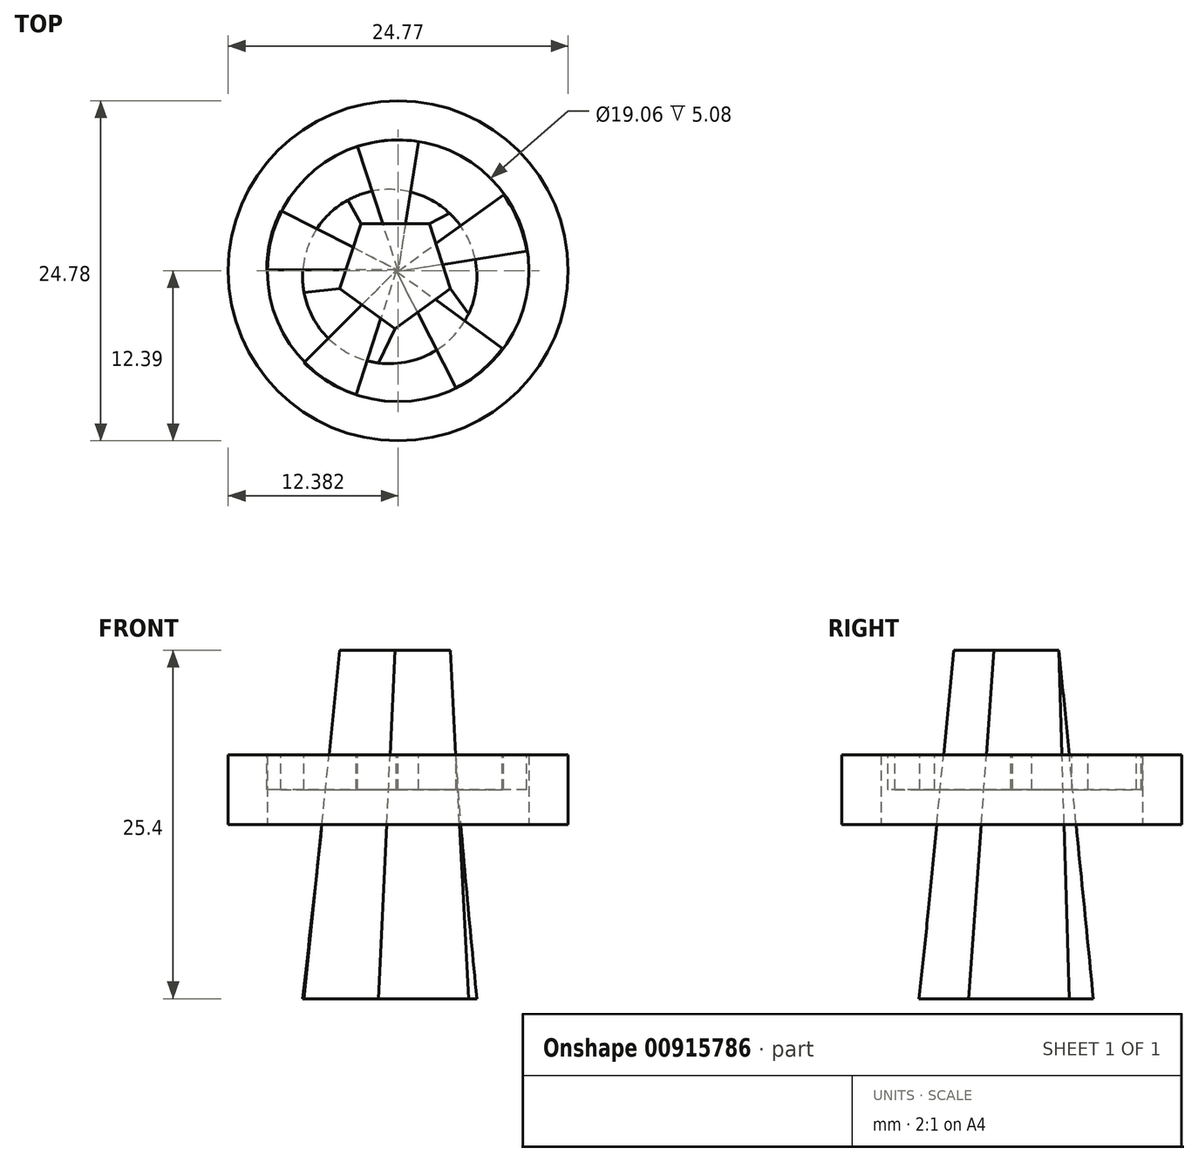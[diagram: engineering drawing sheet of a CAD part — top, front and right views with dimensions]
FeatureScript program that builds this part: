
annotation { "Feature Type Name" : "Feature", "Feature Type Description" : "" }
export const myFeature = defineFeature(function(context is Context, id is Id, definition is map)
    precondition{}
    {
        {
            var Q0;
            Q0=qCreatedBy(makeId("Top.planeOp"),FACE);
            var sketch = newSketch(context, id + "F0", { "sketchPlane" : qUnion([Q0])});
            skCircle(sketch, "E0", {"center": v(-46, -0.42) * mm, "radius": 6.35 * mm});
            skSolve(sketch);
        }
        {
            var Q0;
            Q0=qCreatedBy(makeId("Front.planeOp"),FACE);
            var sketch = newSketch(context, id + "F1", { "sketchPlane" : qUnion([Q0])});
            skLineSegment(sketch, "E1", {"start": v(-45.45, 0) * mm, "end": v(-45.45, 25.4) * mm});
            skLineSegment(sketch, "E2", {"start": v(-45.45, 12.7) * mm, "end": v(-32.74, 12.7) * mm});
            skSolve(sketch);
        }
        {
            var Q0;
            Q0=sQuery(id+"F1.wireOp",EDGE,"E1");
            var Q1;
            Q1=sQuery(id+"F1.wireOp",VERTEX,"E1.end");
            cPlane(context, id + "F2", {"entities" : qUnion([Q0, Q1]), "cplaneType" : CPlaneType.CURVE_POINT, "offset" : 25.4 * mm, "width" : 152.4 * mm, "height" : 152.4 * mm});
        }
        {
            var Q0;
            Q0=qCreatedBy(id+"F2.planeOp",FACE);
            var sketch = newSketch(context, id + "F3", { "sketchPlane" : qUnion([Q0])});
            skCircle(sketch, "E3.cCircle", {"center": v(-45.6, 0) * mm, "radius": 3.43 * mm, "construction": true});
            skLineSegment(sketch, "E3.0", {"start": v(-48.1, 3.43) * mm, "end": v(-43.11, 3.43) * mm});
            skLineSegment(sketch, "E3.1", {"start": v(-43.11, 3.43) * mm, "end": v(-41.58, -1.3) * mm});
            skLineSegment(sketch, "E3.2", {"start": v(-41.58, -1.3) * mm, "end": v(-45.6, -4.23) * mm});
            skLineSegment(sketch, "E3.3", {"start": v(-45.6, -4.23) * mm, "end": v(-49.63, -1.3) * mm});
            skLineSegment(sketch, "E3.4", {"start": v(-49.63, -1.3) * mm, "end": v(-48.1, 3.43) * mm});
            skPoint(sketch, "E3.0.midPoint", {"position": v(-45.6, 3.43) * mm});
            skSolve(sketch);
        }
        {
            var Q0;
            Q0=makeQuery(id+"F0.imprint","IMPRINT",FACE,{"disambiguationData":[TD([[makeQuery(id+"F0.imprint","IMPRINT",EDGE,{"derivedFrom":sQuery(id+"F0.wireOp",EDGE,"E0")}),1.0]])]});
            var Q1;
            Q1=makeQuery(id+"F3.imprint","IMPRINT",FACE,{"disambiguationData":[TD([[makeQuery(id+"F3.imprint","IMPRINT",EDGE,{"derivedFrom":sQuery(id+"F3.wireOp",EDGE,"E3.0")}),-1.0]])]});
            loft(context, id + "F4", {"sheetProfilesArray" : [{ "sheetProfileEntities" : qUnion([Q0]) }, { "sheetProfileEntities" : qUnion([Q1]) }]});
        }
        {
            var Q0;
            Q0=qCreatedBy(makeId("Top.planeOp"),FACE);
            cPlane(context, id + "F5", {"entities" : qUnion([Q0]), "cplaneType" : CPlaneType.OFFSET, "offset" : 12.7 * mm, "width" : 152.4 * mm, "height" : 152.4 * mm});
        }
        {
            var Q0;
            Q0=qCreatedBy(id+"F5.planeOp",FACE);
            var sketch = newSketch(context, id + "F6", { "sketchPlane" : qUnion([Q0])});
            skCircle(sketch, "E4", {"center": v(-45.38, 0) * mm, "radius": 9.53 * mm});
            skCircle(sketch, "E5", {"center": v(-45.38, 0) * mm, "radius": 12.39 * mm});
            skSolve(sketch);
        }
        {
            var Q0;
            Q0=makeQuery(id+"F6.imprint","IMPRINT",FACE,{"disambiguationData":[TD([[makeQuery(id+"F6.imprint","IMPRINT",EDGE,{"derivedFrom":sQuery(id+"F6.wireOp",EDGE,"E4")}),-1.0]])]});
            extrude(context, id + "F7", {"entities" : qUnion([Q0]), "depth" : 5.08 * mm, "offsetDistance" : 25.4 * mm});
        }
        {
            var Q0;
            Q0=makeQuery(id+"F7.opExtrude","CAP_FACE",FACE,{"disambiguationData":[OSD([sQuery(id+"F6.wireOp",EDGE,"E4"),sQuery(id+"F6.wireOp",EDGE,"E5")])],"isStart":false});
            var sketch = newSketch(context, id + "F8", { "sketchPlane" : qUnion([Q0])});
            skLineSegment(sketch, "E6", {"start": v(-43.9, 9.42) * mm, "end": v(-45.38, 0) * mm});
            skLineSegment(sketch, "E7", {"start": v(-45.38, 0) * mm, "end": v(-48.33, 9.06) * mm});
            skSolve(sketch);
        }
        {
            var Q0;
            {var subQ0=sQuery(id+"F8.wireOp",EDGE,"E6");Q0=makeQuery(id+"F8.imprint","IMPRINT",FACE,{"disambiguationData":[TD([[makeQuery(id+"F8.imprint","IMPRINT",EDGE,{"derivedFrom":subQ0}),-1.0]])]});}
            extrude(context, id + "F9", {"entities" : qUnion([Q0]), "oppositeDirection" : true, "depth" : 2.54 * mm, "offsetDistance" : 25.4 * mm});
        }
        {
            var Q0;
            Q0=makeQuery(id+"F9.opExtrude","SWEPT_BODY",BODY,{"disambiguationData":[OSD([sQuery(id+"F6.wireOp",EDGE,"E4"),sQuery(id+"F8.wireOp",EDGE,"E6"),sQuery(id+"F8.wireOp",EDGE,"E7")])]});
            var Q1;
            Q1=sQuery(id+"F1.wireOp",EDGE,"E1");
            circularPattern(context, id + "F10", {"entities" : qUnion([Q0]), "axis" : qUnion([Q1]), "angle" : 360 * degree, "instanceCount" : 5, "equalSpace" : true});
        }
    });
